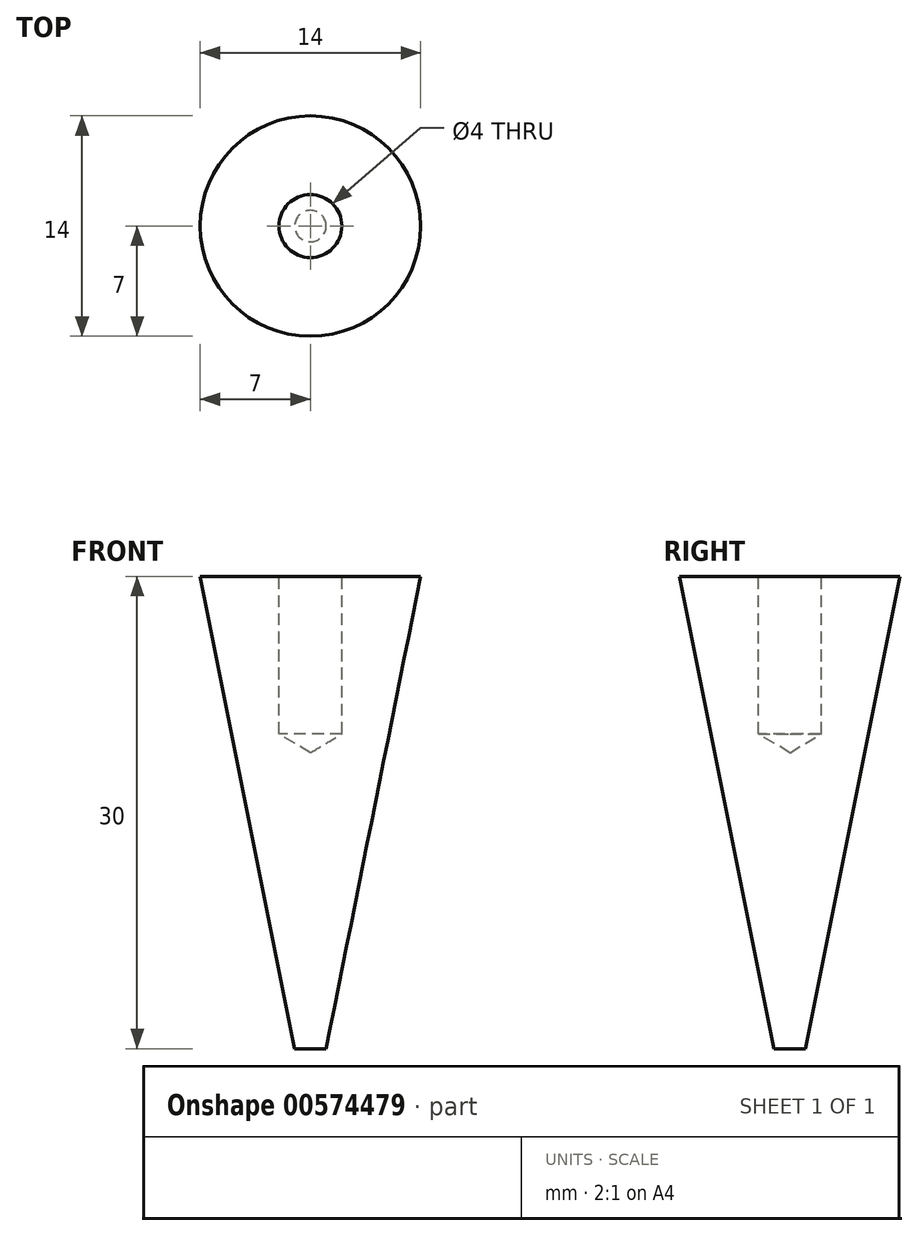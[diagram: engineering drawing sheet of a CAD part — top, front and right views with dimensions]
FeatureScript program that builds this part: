
annotation { "Feature Type Name" : "Feature", "Feature Type Description" : "" }
export const myFeature = defineFeature(function(context is Context, id is Id, definition is map)
    precondition{}
    {
        {
            var Q0;
            Q0=qCreatedBy(makeId("Top.planeOp"),FACE);
            var sketch = newSketch(context, id + "F0", { "sketchPlane" : qUnion([Q0])});
            skCircle(sketch, "E0", {"center": v(0, 0) * mm, "radius": 7 * mm});
            skSolve(sketch);
        }
        {
            var Q0;
            Q0=makeQuery(id+"F0.imprint","IMPRINT",FACE,{"disambiguationData":[TD([[makeQuery(id+"F0.imprint","IMPRINT",EDGE,{"derivedFrom":sQuery(id+"F0.wireOp",EDGE,"E0")}),1.0]])]});
            extrude(context, id + "F1", {"entities" : qUnion([Q0]), "depth" : 30 * mm, "offsetDistance" : 25 * mm});
        }
        {
            var Q0;
            Q0=makeQuery(id+"F1.opExtrude","CAP_FACE",FACE,{"disambiguationData":[OSD([sQuery(id+"F0.wireOp",EDGE,"E0")])],"isStart":false});
            var sketch = newSketch(context, id + "F2", { "sketchPlane" : qUnion([Q0])});
            skPoint(sketch, "E1", {"position": v(0, 0) * mm});
            skSolve(sketch);
        }
        {
            var Q0;
            Q0=sQuery(id+"F2.wireOp",VERTEX,"E1");
            var Q1;
            Q1=makeQuery(id+"F1.opExtrude","SWEPT_BODY",BODY,{"disambiguationData":[OSD([sQuery(id+"F0.wireOp",EDGE,"E0")])]});
            hole(context, id + "F3", {"style" : HoleStyle.SIMPLE, "endStyle" : HoleEndStyle.BLIND, "holeDiameter" : 4 * mm, "holeDepth" : 10 * mm, "isTappedThrough" : true, "tappedDepth" : 12 * mm, "tapClearance" : 3, "locations" : qUnion([Q0]), "scope" : qUnion([Q1])});
        }
        {
            var Q0;
            Q0=makeQuery(id+"F1.opExtrude","CAP_EDGE",EDGE,{"disambiguationData":[OSD([sQuery(id+"F0.wireOp",EDGE,"E0")])],"isStart":true});
            chamfer(context, id + "F4", {"entities" : qUnion([Q0]), "chamferType" : ChamferType.TWO_OFFSETS, "width1" : 30 * mm, "oppositeDirection" : false, "width2" : 6 * mm, "tangentPropagation" : true});
        }
    });
